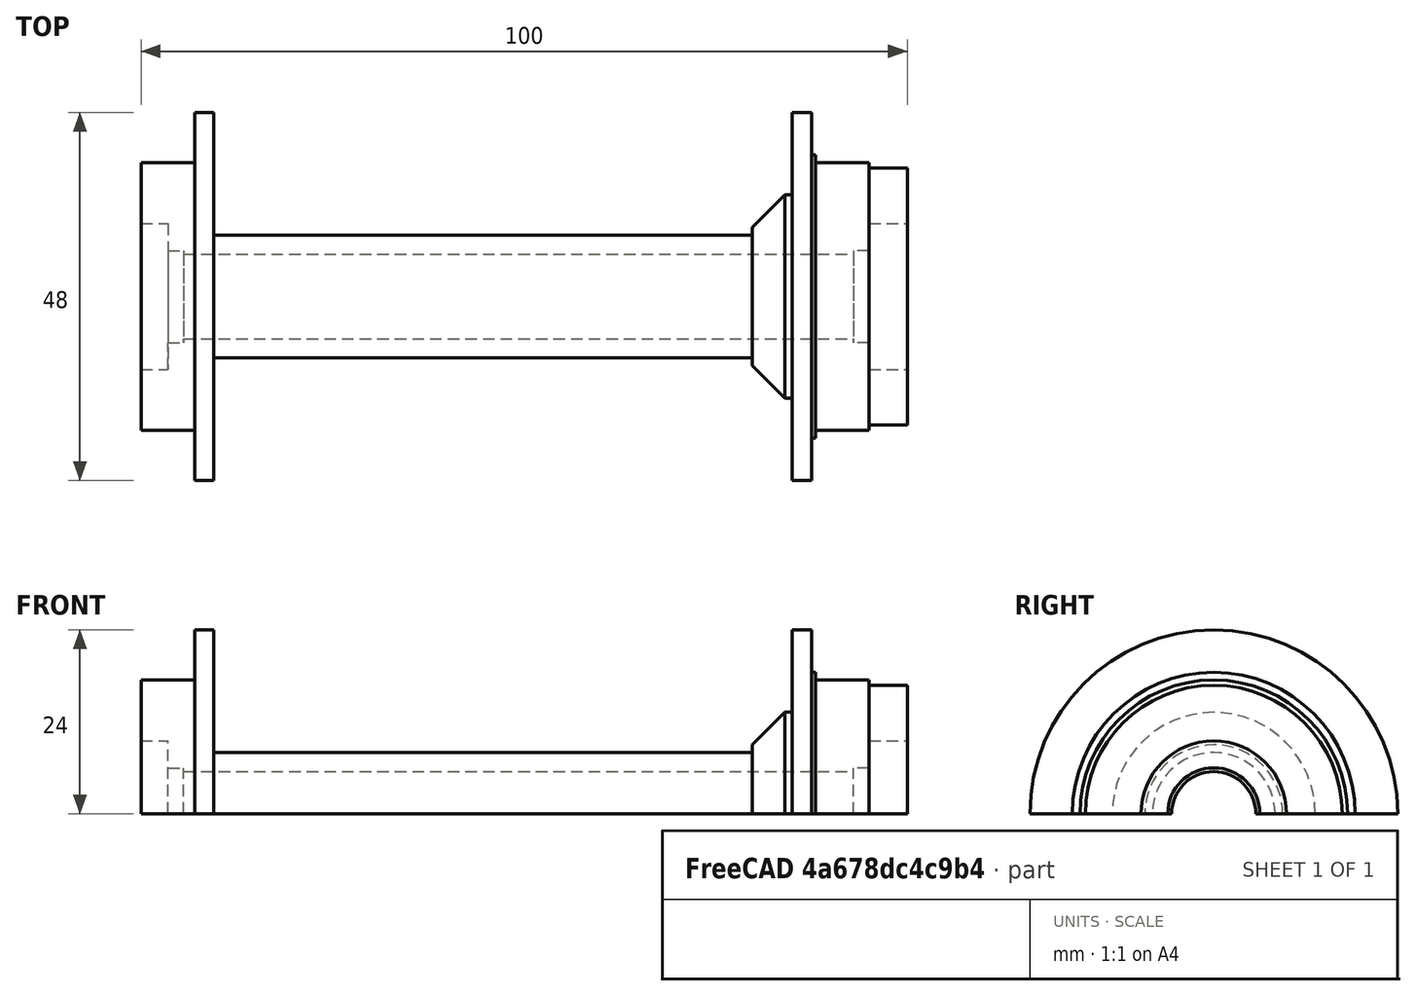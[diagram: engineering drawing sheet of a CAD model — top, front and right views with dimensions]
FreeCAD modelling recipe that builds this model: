
FCSTD DOCUMENT  (FreeCAD 0.16R)
Label: 100mmTandem
License: All rights reserved
LicenseURL: http://en.wikipedia.org/wiki/All_rights_reserved
objects: Sketcher::SketchObject×1, PartDesign::Revolution×1
note: 3 computed .brp shape members not serialized (recipe doc carries the construction recipe); baked Part::Feature solids carry a one-line shape summary decoded from their .brp

FEATURE [Sketcher::SketchObject] Sketch
  sketch-geometry (29):
    g0: LineSegment StartX=-5 StartY=6 StartZ=0 EndX=-5 EndY=9.5 EndZ=0
    g1: LineSegment StartX=-5 StartY=9.5 StartZ=0 EndX=0 EndY=9.5 EndZ=0
    g2: LineSegment StartX=0 StartY=9.5 StartZ=0 EndX=0 EndY=16.76 EndZ=0
    g3: LineSegment StartX=0 StartY=16.76 StartZ=0 EndX=-5 EndY=16.76 EndZ=0
    g4: LineSegment StartX=-5 StartY=16.76 StartZ=0 EndX=-5 EndY=17.46 EndZ=0
    g5: LineSegment StartX=-5 StartY=17.46 StartZ=0 EndX=-12 EndY=17.46 EndZ=0
    g6: LineSegment StartX=-12.0255 StartY=18.46 StartZ=0 EndX=-12.5255 EndY=18.46 EndZ=0
    g7: LineSegment StartX=-12.5255 StartY=18.46 StartZ=0 EndX=-12.5255 EndY=24 EndZ=0
    g8: LineSegment StartX=-12.5255 StartY=24 StartZ=0 EndX=-15.0255 EndY=24 EndZ=0
    g9: LineSegment StartX=-15.0255 StartY=24 StartZ=0 EndX=-15.0255 EndY=13.2426 EndZ=0
    g10: LineSegment StartX=-15.0255 StartY=13.2426 StartZ=0 EndX=-16.0255 EndY=13.2426 EndZ=0
    g11: LineSegment StartX=-16.0255 StartY=13.2426 StartZ=0 EndX=-20.2681 EndY=9 EndZ=0
    g12: LineSegment StartX=-20.2681 StartY=8 StartZ=0 EndX=-75.2574 EndY=8 EndZ=0
    g13: LineSegment StartX=-80.5 StartY=13.2426 StartZ=0 EndX=-80.5 EndY=24 EndZ=0
    g14: LineSegment StartX=-80.5 StartY=24 StartZ=0 EndX=-83 EndY=24 EndZ=0
    g15: LineSegment StartX=-90 StartY=9.5 StartZ=0 EndX=-85 EndY=9.5 EndZ=0
    g16: LineSegment StartX=-85 StartY=9.5 StartZ=0 EndX=-85 EndY=6 EndZ=0
    g17: LineSegment StartX=-85 StartY=6 StartZ=0 EndX=-83 EndY=6 EndZ=0
    g18: LineSegment StartX=-83 StartY=6 StartZ=0 EndX=-83 EndY=5.5 EndZ=0
    g19: LineSegment StartX=-83 StartY=5.5 StartZ=0 EndX=-7 EndY=5.5 EndZ=0
    g20: LineSegment StartX=-5 StartY=6 StartZ=0 EndX=-7 EndY=6 EndZ=0
    g21: LineSegment StartX=-7 StartY=6 StartZ=0 EndX=-7 EndY=5.5 EndZ=0
    g22: LineSegment StartX=-83 StartY=24 StartZ=0 EndX=-83 EndY=17.46 EndZ=0
    g23: LineSegment StartX=-83 StartY=17.46 StartZ=0 EndX=-90 EndY=17.46 EndZ=0
    g24: LineSegment StartX=-90 StartY=17.46 StartZ=0 EndX=-90 EndY=9.5 EndZ=0
    g25: LineSegment StartX=-79.5 StartY=13.2426 StartZ=0 EndX=-75.2574 EndY=9 EndZ=0
    g26: LineSegment StartX=-80.5 StartY=13.2426 StartZ=0 EndX=-79.5 EndY=13.2426 EndZ=0
    g27: LineSegment StartX=-75.2574 StartY=9 StartZ=0 EndX=-75.2574 EndY=8 EndZ=0
    g28: LineSegment StartX=-20.2681 StartY=9 StartZ=0 EndX=-20.2681 EndY=8 EndZ=0
  constraints (86):
    c: Coincident(g0,g1)
    c: Horizontal(g1)
    c: Coincident(g1,g2)
    c: Coincident(g2,g3)
    c: Horizontal(g3)
    c: Coincident(g3,g4)
    c: Coincident(g4,g5)
    c: Coincident(g6,g7)
    c: Vertical(g7)
    c: Coincident(g7,g8)
    c: Horizontal(g8)
    c: Coincident(g8,g9)
    c: Vertical(g9)
    c: Coincident(g9,g10)
    c: Coincident(g10,g11)
    c: Horizontal(g12)
    c: Vertical(g13)
    c: Coincident(g13,g14)
    c: Coincident(g15,g16)
    c: Vertical(g16)
    c: Coincident(g16,g17)
    c: Coincident(g17,g18)
    c: Coincident(g18,g19)
    c: Horizontal(g19)
    c: Coincident(g20,g0)
    c: Coincident(g21,g20)
    c: Coincident(g21,g19)
    c: Equal(g18,g21)
    c: Vertical(g21)
    c: Vertical(g18)
    c: Horizontal(g20)
    c: Horizontal(g10)
    c: Horizontal(g5)
    c: Horizontal(g14)
    c: Horizontal(g15)
    c: DistanceY(g-1,g0) = 6
    c: DistanceY(g-1,g19) = 5.5
    c: DistanceY(g-1,g1) = 9.5
    c: DistanceX(g1,g1) = 5
    c: DistanceY(g-1,g15) = 9.5
    c: DistanceX(g15,g1) = 90
    c: Vertical(g0)
    c: DistanceX(g17,g17) = 2
    c: DistanceX(g20,g20) = 2
    c: Vertical(g2)
    c: DistanceX(g6,g6) = 0.5
    c: Horizontal(g6)
    c: DistanceY(g-1,g4) = 17.46
    c: Vertical(g4)
    c: DistanceX(g8,g8) = 2.5
    c: DistanceY(g-1,g2) = 16.76
    c: DistanceX(g5,g5) = 7
    c: DistanceX(g3,g3) = 5
    c: DistanceY(g5,g6) = 1
    c: DistanceY(g-1,g12) = 8
    c: DistanceX(g14,g14) = 2.5
    c: DistanceY(g-1,g8) = 24
    c: Distance(g10) = 1
    c: Angle(g11) = -2.35619
    c: Distance(g11) = 6
    c: DistanceX(g-1,g1) = 0
    c: Coincident(g14,g22)
    c: Coincident(g22,g23)
    c: Coincident(g23,g24)
    c: Coincident(g15,g24)
    c: Vertical(g24)
    c: Vertical(g22)
    c: Horizontal(g23)
    c: DistanceY(g14) = 24
    c: DistanceY(g23) = 17.46
    c: DistanceX(g23,g23) = 7
    c: DistanceX(g15,g15) = 5
    c: Angle(g25) = -0.785398
    c: Distance(g25) = 6
    c: Horizontal(g26)
    c: DistanceX(g26,g26) = 1
    c: Vertical(g27)
    c: Distance(g27) = 1
    c: Coincident(g27,g25)
    c: Coincident(g26,g25)
    c: Coincident(g26,g13)
    c: Coincident(g27,g12)
    c: Vertical(g28)
    c: Distance(g28) = 1
    c: Coincident(g28,g12)
    c: Coincident(g28,g11)
FEATURE [PartDesign::Revolution] Revolution
  Angle = 180
  Axis = (1,0,0)
  Base = (0,0,0)
  ReferenceAxis = -> Sketch [H_Axis]
  Sketch = -> Sketch
